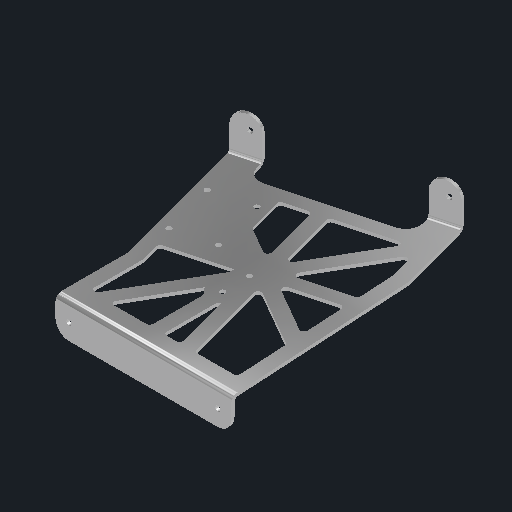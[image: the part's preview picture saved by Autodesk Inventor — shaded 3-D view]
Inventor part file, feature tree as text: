
AUTODESK INVENTOR PART (.ipt)
format: ipt  version: 2024.3 (Build 283343010, 343A)  size: 258,048 bytes
history: native  units: mm (DEFAULTED — no unit token found)
features: sketch x7, other x3, plane x2
ambient origin geometry x8: Origin, YZ Plane, XZ Plane, XY Plane, X Axis, Y Axis, Z Axis, Center Point
bodies: Solid1 (feature_tree)
feature tree (12):
  other  "feeder_side_support_r.ipt"
  other  "Solid1::feeder_side_support_r.ipt"
  other  "TaggingFeature1"
  sketch  "Sketch1"  dims[d0=10.0mm]
  sketch  "Sketch2"  dims[d1=3.048mm]
  sketch  "Sketch3"
  sketch  "Sketch4"
  sketch  "Sketch7"
  sketch  "Sketch8"
  sketch  "Sketch9"
  plane  "Work Plane1"
  plane  "Work Plane2"
